# Revit family: Lavatory-Undercounter_Contemporary_LT481_TOTO
name_source: partatom
category: Plumbing Fixtures
revit_build: Autodesk Revit Architecture 2013 (Build: 20130531_2115(x64)
units: mm (PartAtom-declared; Revit-internal decimal feet)

## types (1)
- LT481
    04 CSI = 22 42 16
    95 CSI = 15410
    ADA Compliant = No
    Assembly Code = D2010310
    Basin Depth = 1' - 3 9/16"
    Basin Width = 1' - 8 5/16"
    CAD Drawing URL = http://assets.totousa.com
    CW Connection = Yes
    CWFU = 0
    Certifications = IAPMO(cUPC), State of Massachusetts , City of Los Angeles, and others
    Code Compliance = UPC, IPC, NSPC, NPC Canada, and others
    Cold Water Connection Radius = 0' - 0 1/4"
    Cold Water Connector = Cold Water Connection
    Color Availability = #01 Cotton, #03 Bone, #11 Colonial White, #12 Sedona Beige, #51 Ebony
    Default Elevation = 0' - 0"
    Depth = 1' - 5 7/8"
    Description = Maris Undercounter Lavatory
    Finish = Vitreous China - TOTO - 01 Cotton
    HW Connection = Yes
    HWFU = 0
    Height = 0' - 6 9/16"
    Hot Water Connection Radius = 0' - 0 1/4"
    Hot Water Connector = Hot Water Connection
    Industry Standards = Meets and exceeds ASME A112.19.2/CSA B45.1
    Manufacturer = TOTO USA, Inc.
    Manufacturer Fax = (770) 282-0002
    Material = Vitreous China
    Model = LT481
    Mounting = Undercounter
    Offset From Countertop = 0' - 1"
    Sanitary Connector = Sanitary Connection
    SanoGloss Available = Yes
    Series = Maris
    Shipping Weight = 22.00 lb
    Sink Configuration = Single Sink
    Sink Type = Lavatory
    Spec Sheet URL = http://assets.totousa.com
    Style = Contemporary
    Subcategory = Lavatories
    Toto BIM Number = BM-00291
    URL = http://www.totousa.com
    Vent Connection = No
    WFU = 0
    Warranty = One Year Limited Warranty
    Warranty URL = http://www.totousa.com
    Waste Connection = Yes
    Waste Connection NPT Radius = 0' - 0 5/8"
    Width = 1' - 10 5/8"
    ecoScorecard Product Page = http://toto.ecoscorecard.com
    ecoScorecard_data = http://toto.ecoscorecard.com

## geometry (parser evidence)
native form markers: Blend x6, Sweep x4
no freeform markers — native parametric forms only
